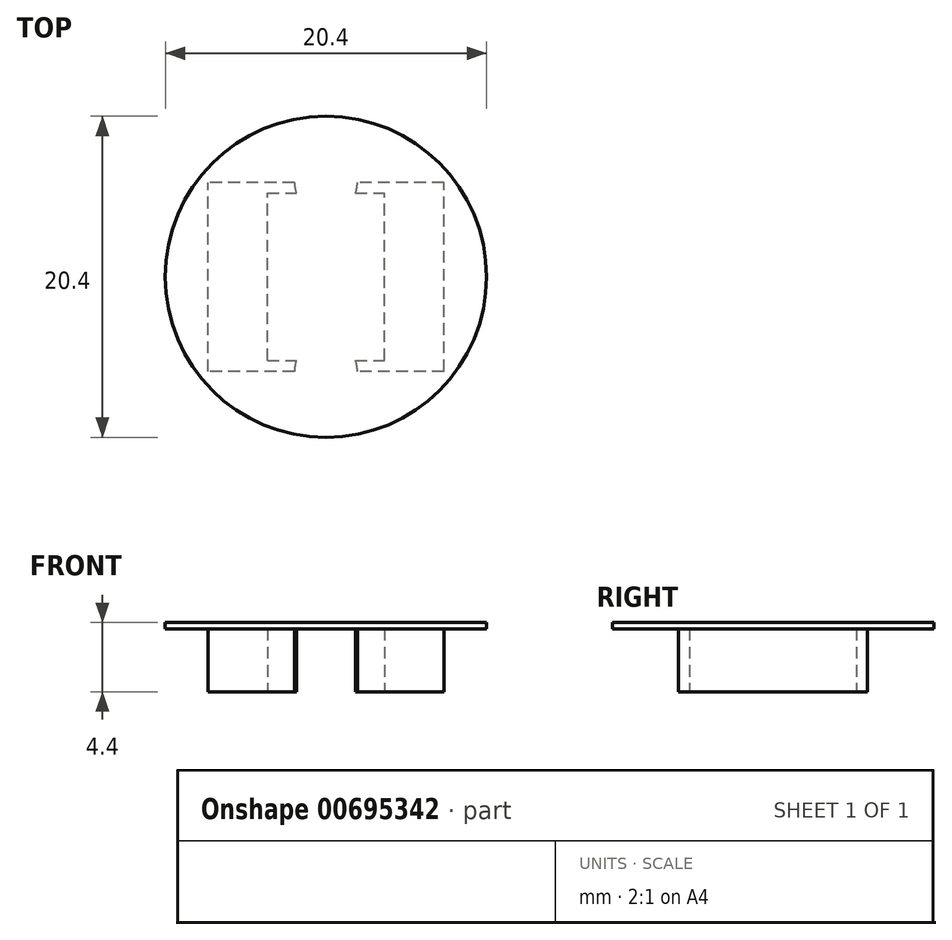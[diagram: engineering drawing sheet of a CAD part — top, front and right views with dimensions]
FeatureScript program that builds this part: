
annotation { "Feature Type Name" : "Feature", "Feature Type Description" : "" }
export const myFeature = defineFeature(function(context is Context, id is Id, definition is map)
    precondition{}
    {
        {
            var Q0;
            Q0=qCreatedBy(makeId("Top.planeOp"),FACE);
            var sketch = newSketch(context, id + "F0", { "sketchPlane" : qUnion([Q0])});
            skLineSegment(sketch, "E0.bottom", {"start": v(7.5, -6) * mm, "end": v(-7.5, -6) * mm});
            skLineSegment(sketch, "E0.top", {"start": v(7.5, 6) * mm, "end": v(-7.5, 6) * mm});
            skLineSegment(sketch, "E0.left", {"start": v(7.5, -6) * mm, "end": v(7.5, 6) * mm});
            skLineSegment(sketch, "E0.right", {"start": v(-7.5, -6) * mm, "end": v(-7.5, 6) * mm});
            skPoint(sketch, "E0.middle", {"position": v(0, 0) * mm});
            skCircle(sketch, "E1", {"center": v(0, 6) * mm, "radius": 2 * mm});
            skCircle(sketch, "E2", {"center": v(0, -6) * mm, "radius": 2 * mm});
            skSolve(sketch);
        }
        {
            var Q0;
            {var subQ0=sQuery(id+"F0.wireOp",EDGE,"E1");var subQ1=sQuery(id+"F0.wireOp",EDGE,"E0.top");var subQ2=makeQuery(id+"F0.imprint","INTERSECT",VERTEX,{"disambiguationData":[OD(0.0)],"derivedFrom":[subQ1,subQ0]});Q0=makeQuery(id+"F0.imprint","IMPRINT",FACE,{"disambiguationData":[TD([[makeQuery(id+"F0.imprint","IMPRINT",EDGE,{"disambiguationData":[TD([[subQ2,-1.0]])],"derivedFrom":subQ1}),-1.0]])]});}
            var Q1;
            {var subQ0=sQuery(id+"F0.wireOp",EDGE,"E1");var subQ1=sQuery(id+"F0.wireOp",EDGE,"E0.top");var subQ2=makeQuery(id+"F0.imprint","INTERSECT",VERTEX,{"disambiguationData":[OD(0.0)],"derivedFrom":[subQ1,subQ0]});Q1=makeQuery(id+"F0.imprint","IMPRINT",FACE,{"disambiguationData":[TD([[makeQuery(id+"F0.imprint","IMPRINT",EDGE,{"disambiguationData":[TD([[subQ2,-1.0]])],"derivedFrom":subQ1}),1.0]])]});}
            var Q2;
            {var subQ0=sQuery(id+"F0.wireOp",EDGE,"E2");var subQ1=sQuery(id+"F0.wireOp",EDGE,"E0.bottom");var subQ2=makeQuery(id+"F0.imprint","INTERSECT",VERTEX,{"disambiguationData":[OD(0.0)],"derivedFrom":[subQ1,subQ0]});Q2=makeQuery(id+"F0.imprint","IMPRINT",FACE,{"disambiguationData":[TD([[makeQuery(id+"F0.imprint","IMPRINT",EDGE,{"disambiguationData":[TD([[subQ2,-1.0]])],"derivedFrom":subQ1}),-1.0]])]});}
            var Q3;
            {var subQ0=sQuery(id+"F0.wireOp",EDGE,"E2");var subQ1=sQuery(id+"F0.wireOp",EDGE,"E0.bottom");var subQ2=makeQuery(id+"F0.imprint","INTERSECT",VERTEX,{"disambiguationData":[OD(0.0)],"derivedFrom":[subQ1,subQ0]});Q3=makeQuery(id+"F0.imprint","IMPRINT",FACE,{"disambiguationData":[TD([[makeQuery(id+"F0.imprint","IMPRINT",EDGE,{"disambiguationData":[TD([[subQ2,-1.0]])],"derivedFrom":subQ1}),1.0]])]});}
            extrude(context, id + "F1", {"entities" : qUnion([Q0, Q1, Q2, Q3]), "depth" : 5 * mm, "offsetDistance" : 25 * mm});
        }
        {
            var Q0;
            {var subQ0=sQuery(id+"F0.wireOp",EDGE,"E1");var subQ1=sQuery(id+"F0.wireOp",EDGE,"E0.top");var subQ2=makeQuery(id+"F0.imprint","INTERSECT",VERTEX,{"disambiguationData":[OD(0.0)],"derivedFrom":[subQ1,subQ0]});Q0=makeQuery(id+"F0.imprint","IMPRINT",FACE,{"disambiguationData":[TD([[makeQuery(id+"F0.imprint","IMPRINT",EDGE,{"disambiguationData":[TD([[subQ2,-1.0]])],"derivedFrom":subQ1}),1.0]])]});}
            var Q1;
            {var subQ0=sQuery(id+"F0.wireOp",EDGE,"E2");var subQ1=sQuery(id+"F0.wireOp",EDGE,"E0.bottom");var subQ2=makeQuery(id+"F0.imprint","INTERSECT",VERTEX,{"disambiguationData":[OD(0.0)],"derivedFrom":[subQ1,subQ0]});Q1=makeQuery(id+"F0.imprint","IMPRINT",FACE,{"disambiguationData":[TD([[makeQuery(id+"F0.imprint","IMPRINT",EDGE,{"disambiguationData":[TD([[subQ2,-1.0]])],"derivedFrom":subQ1}),-1.0]])]});}
            extrude(context, id + "F2", {"entities" : qUnion([Q0, Q1]), "operationType" : NewBodyOperationType.REMOVE, "depth" : 1 * mm, "offsetDistance" : 25 * mm});
        }
        {
            var Q0;
            {var subQ0=sQuery(id+"F0.wireOp",EDGE,"E0.left");Q0=makeQuery(id+"F0.imprint","IMPRINT",FACE,{"disambiguationData":[TD([[makeQuery(id+"F0.imprint","IMPRINT",EDGE,{"derivedFrom":subQ0}),1.0]])]});}
            var sketch = newSketch(context, id + "F3", { "sketchPlane" : qUnion([Q0])});
            skLineSegment(sketch, "E3.bottom", {"start": v(3.72, 5.3) * mm, "end": v(-3.72, 5.3) * mm});
            skLineSegment(sketch, "E3.top", {"start": v(3.72, -5.3) * mm, "end": v(-3.72, -5.3) * mm});
            skLineSegment(sketch, "E3.left", {"start": v(3.72, 5.3) * mm, "end": v(3.72, -5.3) * mm});
            skLineSegment(sketch, "E3.right", {"start": v(-3.72, 5.3) * mm, "end": v(-3.72, -5.3) * mm});
            skPoint(sketch, "E3.middle", {"position": v(0, 0) * mm});
            skSolve(sketch);
        }
        {
            var Q0;
            Q0 = qSketchRegion(id + "F3", true);
            extrude(context, id + "F4", {"entities" : qUnion([Q0]), "operationType" : NewBodyOperationType.REMOVE, "depth" : 25 * mm, "offsetDistance" : 25 * mm});
        }
        {
            var Q0;
            Q0=makeQuery(id+"F1.opExtrude","CAP_FACE",FACE,{"disambiguationData":[OSD([sQuery(id+"F0.wireOp",EDGE,"E1")])],"isStart":false});
            var sketch = newSketch(context, id + "F5", { "sketchPlane" : qUnion([Q0])});
            skCircle(sketch, "E4", {"center": v(0, 0) * mm, "radius": 10.2 * mm});
            skSolve(sketch);
        }
        {
            var Q0;
            Q0 = qSketchRegion(id + "F5", true);
            extrude(context, id + "F6", {"entities" : qUnion([Q0]), "depth" : .4 * mm, "offsetDistance" : 25 * mm});
        }
    });
